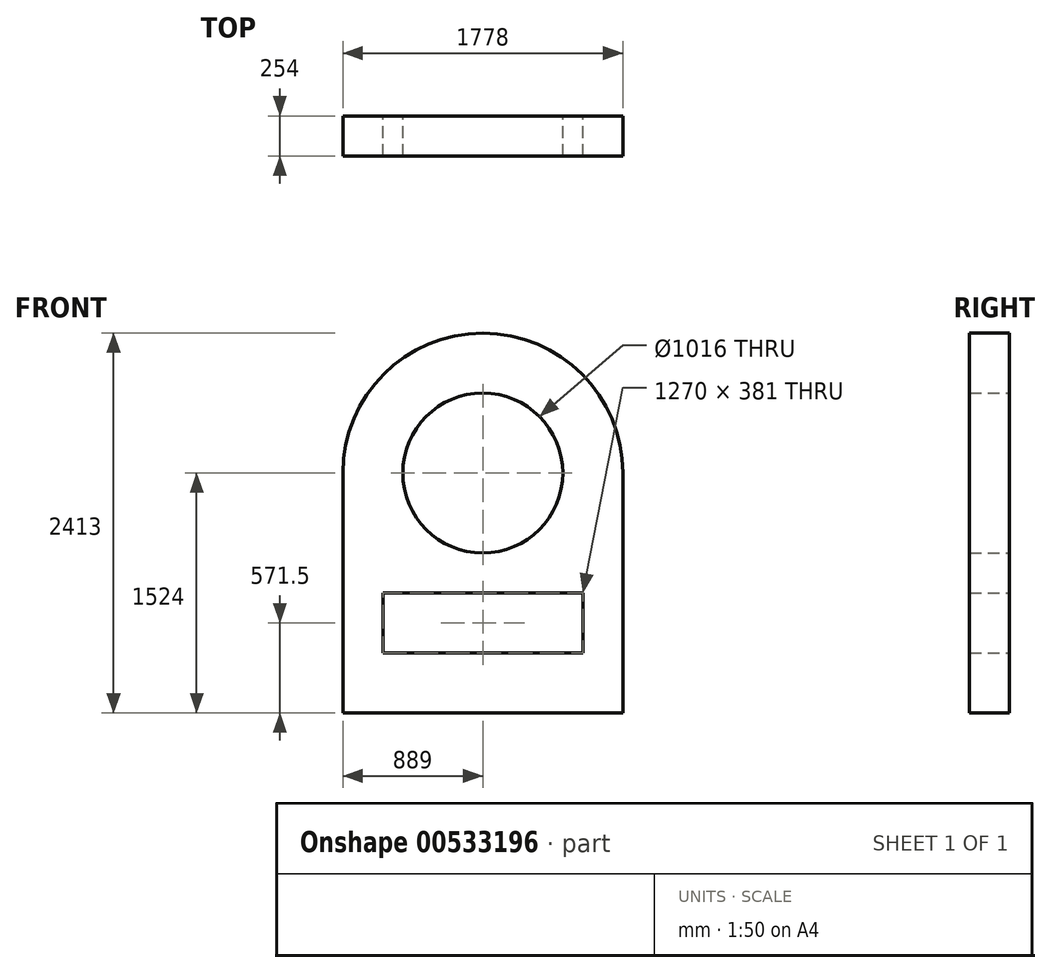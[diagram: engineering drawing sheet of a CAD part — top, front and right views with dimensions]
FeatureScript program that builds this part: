
annotation { "Feature Type Name" : "Feature", "Feature Type Description" : "" }
export const myFeature = defineFeature(function(context is Context, id is Id, definition is map)
    precondition{}
    {
        {
            var Q0;
            Q0=qCreatedBy(makeId("Front.planeOp"),FACE);
            var sketch = newSketch(context, id + "F0", { "sketchPlane" : qUnion([Q0])});
            skLineSegment(sketch, "E0", {"start": v(0, 0) * mm, "end": v(1778, 0) * mm});
            skLineSegment(sketch, "E1", {"start": v(1778, 0) * mm, "end": v(1778, 1524) * mm});
            skLineSegment(sketch, "E2", {"start": v(0, 0) * mm, "end": v(0, 1524) * mm});
            skArc(sketch, "E3", {"start": v(1778, 1524) * mm, "mid": v(889, 2413) * mm, "end": v(0, 1524) * mm});
            skCircle(sketch, "E4", {"center": v(889, 1524) * mm, "radius": 508 * mm});
            skLineSegment(sketch, "E5", {"start": v(254, 762) * mm, "end": v(1524, 762) * mm});
            skLineSegment(sketch, "E6", {"start": v(1524, 762) * mm, "end": v(1524, 381) * mm});
            skLineSegment(sketch, "E7", {"start": v(254, 762) * mm, "end": v(254, 381) * mm});
            skLineSegment(sketch, "E8", {"start": v(254, 381) * mm, "end": v(1524, 381) * mm});
            skSolve(sketch);
        }
        {
            var Q0;
            Q0=makeQuery(id+"F0.imprint","IMPRINT",FACE,{"disambiguationData":[TD([[makeQuery(id+"F0.imprint","IMPRINT",EDGE,{"derivedFrom":sQuery(id+"F0.wireOp",EDGE,"E0")}),1.0]])]});
            extrude(context, id + "F1", {"entities" : qUnion([Q0]), "depth" : 254 * mm, "offsetDistance" : 25.4 * mm});
        }
    });
